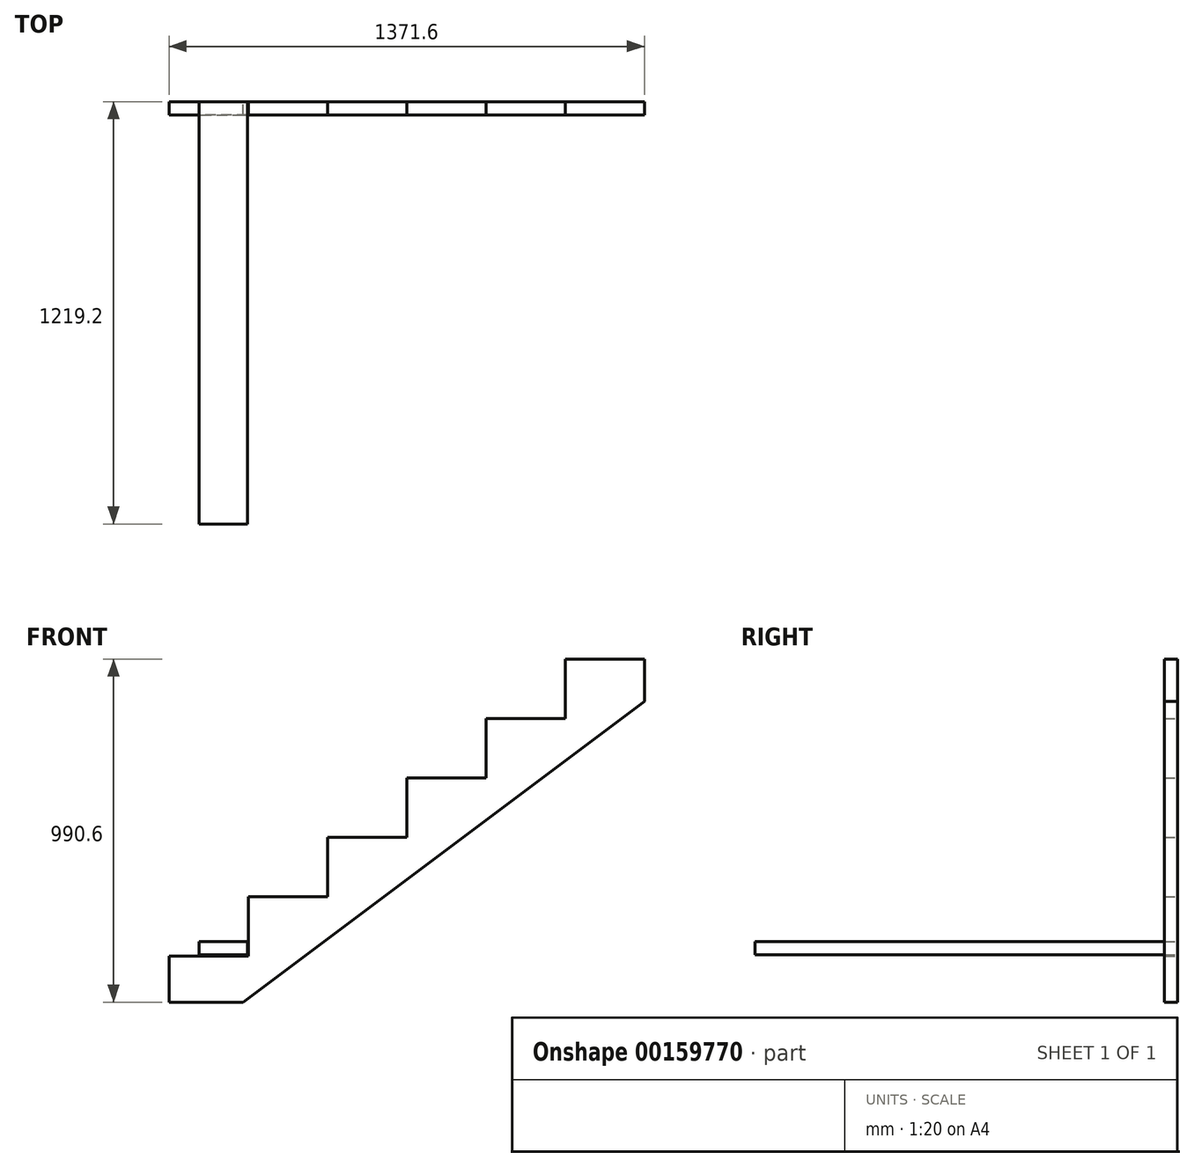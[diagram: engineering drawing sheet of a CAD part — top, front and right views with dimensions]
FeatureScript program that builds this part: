
annotation { "Feature Type Name" : "Feature", "Feature Type Description" : "" }
export const myFeature = defineFeature(function(context is Context, id is Id, definition is map)
    precondition{}
    {
        {
            var Q0;
            Q0=qCreatedBy(makeId("Front.planeOp"),FACE);
            var sketch = newSketch(context, id + "F0", { "sketchPlane" : qUnion([Q0])});
            skLineSegment(sketch, "E0", {"start": v(-2691.27, -1030.62) * mm, "end": v(2691.87, -1030.62) * mm, "construction": true});
            skLineSegment(sketch, "E1", {"start": v(520.2, -1030.62) * mm, "end": v(520.2, -1.92) * mm, "construction": true});
            skLineSegment(sketch, "E2", {"start": v(520.2, -1.92) * mm, "end": v(291.6, -1.92) * mm});
            skLineSegment(sketch, "E3", {"start": v(291.6, -1.92) * mm, "end": v(291.6, -173.37) * mm});
            skLineSegment(sketch, "E4", {"start": v(291.6, -173.37) * mm, "end": v(63, -173.37) * mm});
            skLineSegment(sketch, "E5", {"start": v(63, -173.37) * mm, "end": v(63, -344.82) * mm});
            skLineSegment(sketch, "E6", {"start": v(63, -344.82) * mm, "end": v(-165.6, -344.82) * mm});
            skLineSegment(sketch, "E7", {"start": v(-165.6, -344.82) * mm, "end": v(-165.6, -516.27) * mm});
            skLineSegment(sketch, "E8", {"start": v(-165.6, -516.27) * mm, "end": v(-394.2, -516.27) * mm});
            skLineSegment(sketch, "E9", {"start": v(-394.2, -516.27) * mm, "end": v(-394.2, -687.72) * mm});
            skLineSegment(sketch, "E10", {"start": v(-394.2, -687.72) * mm, "end": v(-622.8, -687.72) * mm});
            skLineSegment(sketch, "E11", {"start": v(-622.8, -687.72) * mm, "end": v(-622.8, -859.17) * mm});
            skLineSegment(sketch, "E12", {"start": v(-622.8, -859.17) * mm, "end": v(-851.4, -859.17) * mm});
            skLineSegment(sketch, "E13", {"start": v(-851.4, -859.17) * mm, "end": v(-851.4, -992.52) * mm});
            skLineSegment(sketch, "E14", {"start": v(-851.4, -1030.62) * mm, "end": v(520.2, -1.92) * mm, "construction": true});
            skLineSegment(sketch, "E15", {"start": v(63, -173.37) * mm, "end": v(203.96, -361.33) * mm, "construction": true});
            skLineSegment(sketch, "E16", {"start": v(-637.62, -992.52) * mm, "end": v(520.2, -124.16) * mm});
            skLineSegment(sketch, "E17", {"start": v(-851.4, -992.52) * mm, "end": v(-637.62, -992.52) * mm});
            skLineSegment(sketch, "E18", {"start": v(520.2, -124.16) * mm, "end": v(520.2, -1.92) * mm});
            skSolve(sketch);
        }
        {
            var Q0;
            Q0=makeQuery(id+"F0.imprint","IMPRINT",FACE,{"disambiguationData":[TD([[makeQuery(id+"F0.imprint","IMPRINT",EDGE,{"derivedFrom":sQuery(id+"F0.wireOp",EDGE,"E2")}),1.0]])]});
            extrude(context, id + "F1", {"entities" : qUnion([Q0]), "depth" : 38.1 * mm});
        }
        {
            var Q0;
            Q0=qCreatedBy(makeId("Front.planeOp"),FACE);
            var sketch = newSketch(context, id + "F2", { "sketchPlane" : qUnion([Q0])});
            skLineSegment(sketch, "E19.bottom", {"start": v(-624.78, -855.46) * mm, "end": v(-764.48, -855.46) * mm});
            skLineSegment(sketch, "E19.top", {"start": v(-624.78, -817.36) * mm, "end": v(-764.48, -817.36) * mm});
            skLineSegment(sketch, "E19.left", {"start": v(-624.78, -855.46) * mm, "end": v(-624.78, -817.36) * mm});
            skLineSegment(sketch, "E19.right", {"start": v(-764.48, -855.46) * mm, "end": v(-764.48, -817.36) * mm});
            skSolve(sketch);
        }
        {
            var Q0;
            Q0 = qSketchRegion(id + "F2", true);
            extrude(context, id + "F3", {"entities" : qUnion([Q0]), "depth" : 1219.2 * mm});
        }
    });
